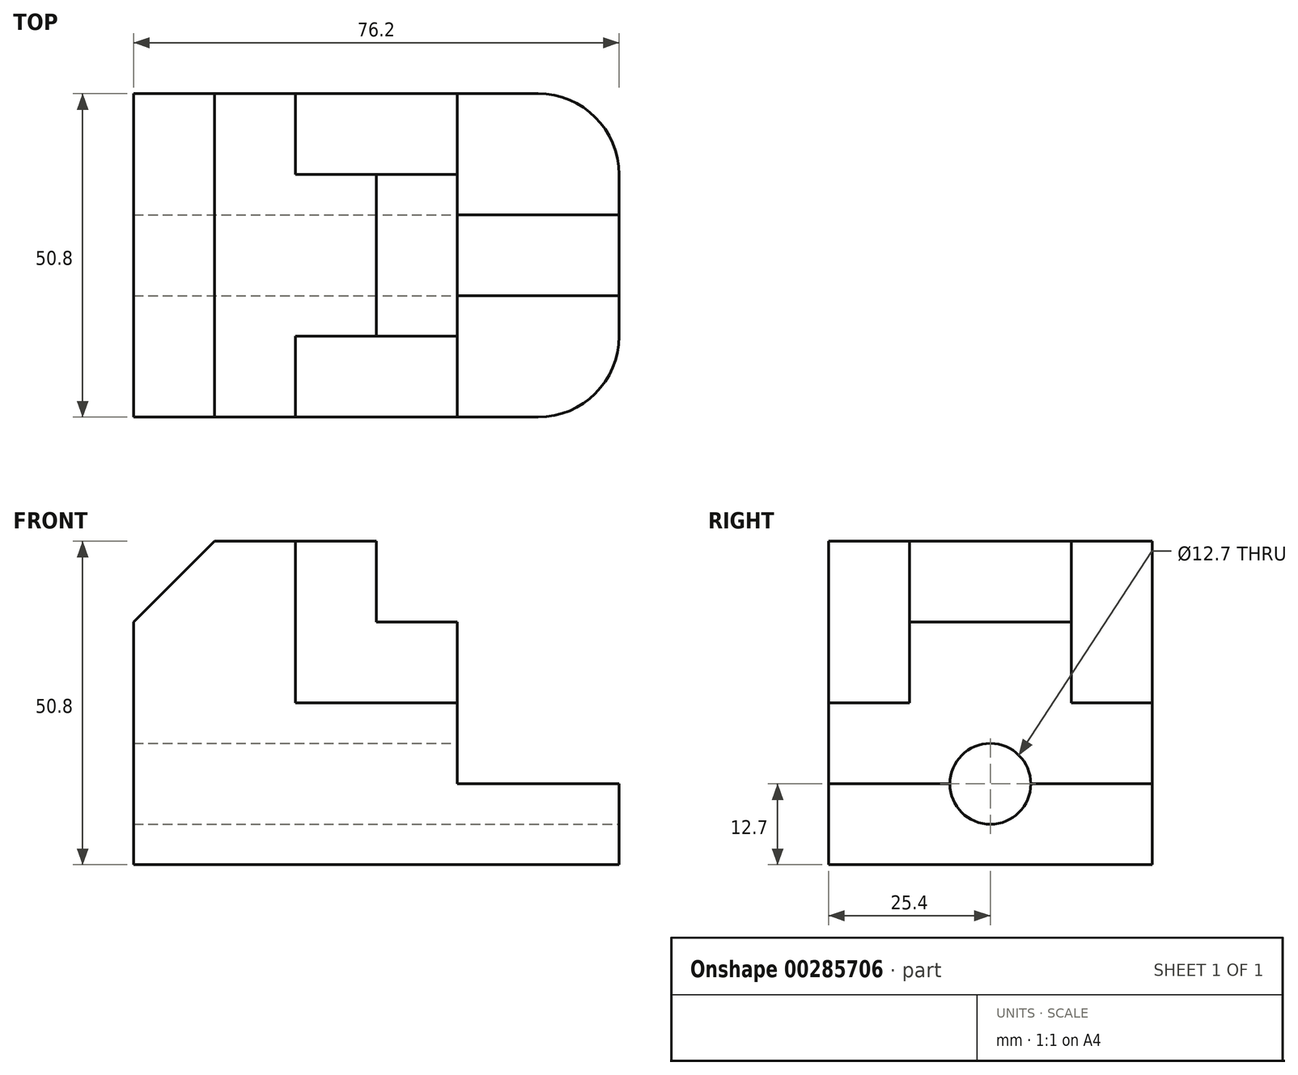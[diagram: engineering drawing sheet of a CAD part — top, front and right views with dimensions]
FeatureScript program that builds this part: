
annotation { "Feature Type Name" : "Feature", "Feature Type Description" : "" }
export const myFeature = defineFeature(function(context is Context, id is Id, definition is map)
    precondition{}
    {
        {
            var Q0;
            Q0=qCreatedBy(makeId("Front.planeOp"),FACE);
            var sketch = newSketch(context, id + "F0", { "sketchPlane" : qUnion([Q0])});
            skLineSegment(sketch, "E0", {"start": v(0, 0) * mm, "end": v(0, 38.1) * mm});
            skLineSegment(sketch, "E1", {"start": v(0, 0) * mm, "end": v(76.2, 0) * mm});
            skLineSegment(sketch, "E2", {"start": v(76.2, 0) * mm, "end": v(76.2, 12.7) * mm});
            skLineSegment(sketch, "E3", {"start": v(76.2, 12.7) * mm, "end": v(50.8, 12.7) * mm});
            skLineSegment(sketch, "E4", {"start": v(50.8, 12.7) * mm, "end": v(50.8, 25.4) * mm});
            skLineSegment(sketch, "E5", {"start": v(50.8, 25.4) * mm, "end": v(25.4, 25.4) * mm});
            skLineSegment(sketch, "E6", {"start": v(25.4, 25.4) * mm, "end": v(25.4, 50.8) * mm});
            skLineSegment(sketch, "E7", {"start": v(25.4, 50.8) * mm, "end": v(12.7, 50.8) * mm});
            skLineSegment(sketch, "E8", {"start": v(12.7, 50.8) * mm, "end": v(0, 38.1) * mm});
            skLineSegment(sketch, "E9", {"start": v(25.4, 50.8) * mm, "end": v(38.1, 50.8) * mm});
            skLineSegment(sketch, "E10", {"start": v(38.1, 50.8) * mm, "end": v(38.1, 38.1) * mm});
            skLineSegment(sketch, "E11", {"start": v(38.1, 38.1) * mm, "end": v(50.8, 38.1) * mm});
            skLineSegment(sketch, "E12", {"start": v(50.8, 38.1) * mm, "end": v(50.8, 25.4) * mm});
            skLineSegment(sketch, "E13", {"start": v(38.1, 50.8) * mm, "end": v(50.8, 50.8) * mm});
            skLineSegment(sketch, "E14", {"start": v(50.8, 50.8) * mm, "end": v(50.8, 38.1) * mm});
            skSolve(sketch);
        }
        {
            var Q0;
            Q0 = qSketchRegion(id + "F0", true);
            extrude(context, id + "F1", {"entities" : qUnion([Q0]), "depth" : 50.8 * mm});
        }
        {
            var Q0;
            Q0=makeQuery(id+"F1.opExtrude","SWEPT_FACE",FACE,{"disambiguationData":[OSD([sQuery(id+"F0.wireOp",EDGE,"E7"),sQuery(id+"F0.wireOp",EDGE,"E9"),sQuery(id+"F0.wireOp",EDGE,"E13")])]});
            var sketch = newSketch(context, id + "F2", { "sketchPlane" : qUnion([Q0])});
            skLineSegment(sketch, "E15.bottom", {"start": v(50.8, -50.8) * mm, "end": v(25.4, -50.8) * mm});
            skLineSegment(sketch, "E15.left", {"start": v(50.8, -50.8) * mm, "end": v(50.8, -38.1) * mm});
            skLineSegment(sketch, "E15.right", {"start": v(25.4, -50.8) * mm, "end": v(25.4, -38.1) * mm});
            skLineSegment(sketch, "E16.bottom", {"start": v(50.8, 0) * mm, "end": v(25.4, 0) * mm});
            skLineSegment(sketch, "E16.top", {"start": v(50.8, -12.7) * mm, "end": v(25.4, -12.7) * mm});
            skLineSegment(sketch, "E16.left", {"start": v(50.8, 0) * mm, "end": v(50.8, -12.7) * mm});
            skLineSegment(sketch, "E16.right", {"start": v(25.4, 0) * mm, "end": v(25.4, -12.7) * mm});
            skLineSegment(sketch, "E17.top", {"start": v(25.4, -50.8) * mm, "end": v(38.1, -50.8) * mm});
            skLineSegment(sketch, "E17.left", {"start": v(25.4, -38.1) * mm, "end": v(25.4, -50.8) * mm});
            skLineSegment(sketch, "E18.bottom", {"start": v(25.4, 0) * mm, "end": v(38.1, 0) * mm});
            skLineSegment(sketch, "E18.top", {"start": v(25.4, -12.7) * mm, "end": v(38.1, -12.7) * mm});
            skLineSegment(sketch, "E18.right", {"start": v(38.1, 0) * mm, "end": v(38.1, -12.7) * mm});
            skLineSegment(sketch, "E19.bottom", {"start": v(38.1, -50.8) * mm, "end": v(25.4, -50.8) * mm});
            skLineSegment(sketch, "E20", {"start": v(25.4, -38.1) * mm, "end": v(50.8, -38.1) * mm});
            skLineSegment(sketch, "E21", {"start": v(38.1, -50.8) * mm, "end": v(38.1, -38.1) * mm});
            skLineSegment(sketch, "E22", {"start": v(38.1, -38.1) * mm, "end": v(38.1, -12.7) * mm});
            skSolve(sketch);
        }
        {
            var Q0;
            Q0=makeQuery(id+"F2.imprint","IMPRINT",FACE,{"disambiguationData":[TD([[makeQuery(id+"F2.imprint","IMPRINT",EDGE,{"derivedFrom":sQuery(id+"F2.wireOp",EDGE,"E15.bottom")}),-1.0]])]});
            var Q1;
            Q1=makeQuery(id+"F2.imprint","IMPRINT",FACE,{"disambiguationData":[TD([[makeQuery(id+"F2.imprint","IMPRINT",EDGE,{"derivedFrom":sQuery(id+"F2.wireOp",EDGE,"E16.bottom")}),1.0]])]});
            var Q2;
            Q2=makeQuery(id+"F2.imprint","IMPRINT",FACE,{"disambiguationData":[TD([[makeQuery(id+"F2.imprint","IMPRINT",EDGE,{"derivedFrom":sQuery(id+"F2.wireOp",EDGE,"E19.bottom")}),-1.0]])]});
            var Q3;
            Q3=makeQuery(id+"F2.imprint","IMPRINT",FACE,{"disambiguationData":[TD([[makeQuery(id+"F2.imprint","IMPRINT",EDGE,{"derivedFrom":sQuery(id+"F2.wireOp",EDGE,"E18.bottom")}),1.0]])]});
            extrude(context, id + "F3", {"entities" : qUnion([Q0, Q1, Q2, Q3]), "operationType" : NewBodyOperationType.REMOVE, "oppositeDirection" : true, "depth" : 25.4 * mm});
        }
        {
            var Q0;
            {var subQ0=sQuery(id+"F2.wireOp",EDGE,"E16.top");Q0=makeQuery(id+"F2.imprint","IMPRINT",FACE,{"disambiguationData":[TD([[makeQuery(id+"F2.imprint","IMPRINT",EDGE,{"derivedFrom":subQ0}),1.0]])]});}
            extrude(context, id + "F4", {"entities" : qUnion([Q0]), "operationType" : NewBodyOperationType.REMOVE, "oppositeDirection" : true, "depth" : 12.7 * mm});
        }
        {
            var Q0;
            Q0=makeQuery(id+"F1.opExtrude","SWEPT_FACE",FACE,{"disambiguationData":[OSD([sQuery(id+"F0.wireOp",EDGE,"E3")])]});
            var sketch = newSketch(context, id + "F5", { "sketchPlane" : qUnion([Q0])});
            skArc(sketch, "E23", {"start": v(63.5, -50.8) * mm, "mid": v(72.48, -47.08) * mm, "end": v(76.2, -38.1) * mm});
            skArc(sketch, "E24", {"start": v(76.2, -12.7) * mm, "mid": v(72.48, -3.72) * mm, "end": v(63.5, 0) * mm});
            skLineSegment(sketch, "E25", {"start": v(76.2, -38.1) * mm, "end": v(76.2, -12.7) * mm});
            skLineSegment(sketch, "E26", {"start": v(76.2, -38.1) * mm, "end": v(76.2, -50.8) * mm});
            skLineSegment(sketch, "E27", {"start": v(76.2, -50.8) * mm, "end": v(63.5, -50.8) * mm});
            skLineSegment(sketch, "E28", {"start": v(76.2, -12.7) * mm, "end": v(76.2, 0) * mm});
            skLineSegment(sketch, "E29", {"start": v(76.2, 0) * mm, "end": v(63.5, 0) * mm});
            skSolve(sketch);
        }
        {
            var Q0;
            Q0 = qSketchRegion(id + "F5", true);
            extrude(context, id + "F6", {"entities" : qUnion([Q0]), "operationType" : NewBodyOperationType.REMOVE, "oppositeDirection" : true, "depth" : 12.7 * mm});
        }
        {
            var Q0;
            Q0=makeQuery(id+"F1.opExtrude","SWEPT_FACE",FACE,{"disambiguationData":[OSD([sQuery(id+"F0.wireOp",EDGE,"E2")])]});
            var sketch = newSketch(context, id + "F7", { "sketchPlane" : qUnion([Q0])});
            skCircle(sketch, "E30", {"center": v(-25.4, 12.7) * mm, "radius": 6.35 * mm});
            skSolve(sketch);
        }
        {
            var Q0;
            Q0 = qSketchRegion(id + "F7", true);
            extrude(context, id + "F8", {"entities" : qUnion([Q0]), "operationType" : NewBodyOperationType.REMOVE, "oppositeDirection" : true, "depth" : 76.2 * mm});
        }
    });
